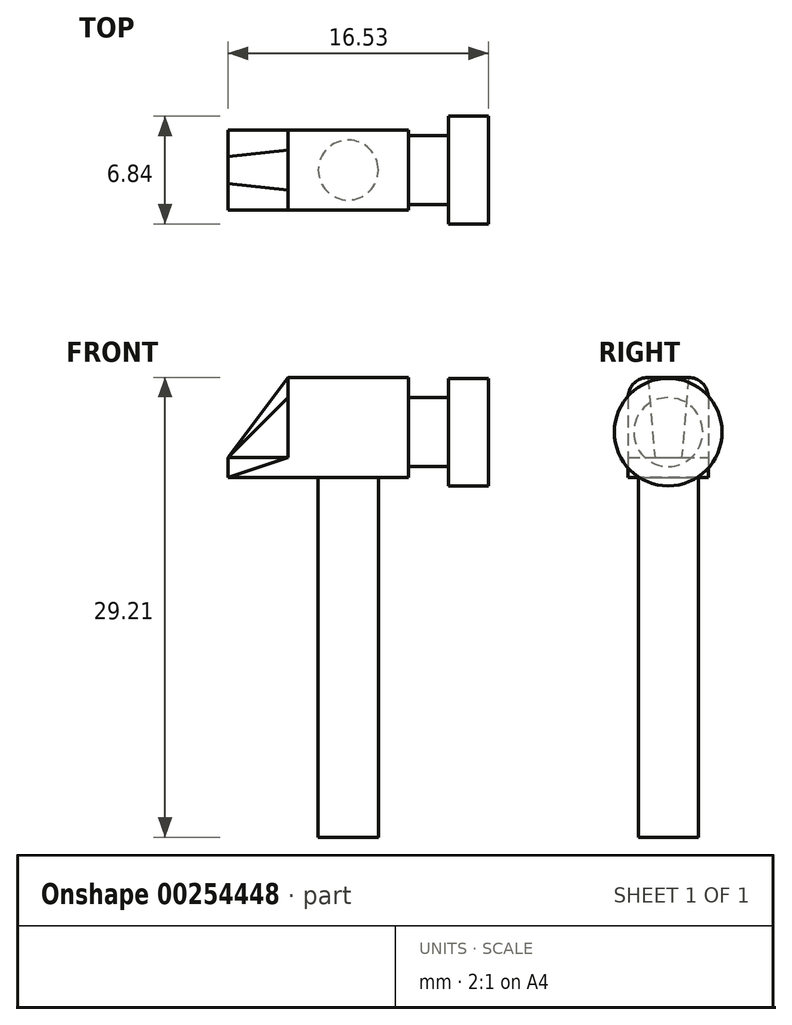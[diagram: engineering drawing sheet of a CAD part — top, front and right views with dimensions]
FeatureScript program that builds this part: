
annotation { "Feature Type Name" : "Feature", "Feature Type Description" : "" }
export const myFeature = defineFeature(function(context is Context, id is Id, definition is map)
    precondition{}
    {
        {
            var Q0;
            Q0=qCreatedBy(makeId("Front.planeOp"),FACE);
            var sketch = newSketch(context, id + "F0", { "sketchPlane" : qUnion([Q0])});
            skLineSegment(sketch, "E0.bottom", {"start": v(0, 0) * mm, "end": v(1.9, 0) * mm});
            skLineSegment(sketch, "E0.top", {"start": v(0, 22.86) * mm, "end": v(1.9, 22.86) * mm});
            skLineSegment(sketch, "E0.left", {"start": v(0, 0) * mm, "end": v(0, 22.86) * mm});
            skLineSegment(sketch, "E0.right", {"start": v(1.9, 0) * mm, "end": v(1.9, 22.86) * mm});
            skSolve(sketch);
        }
        {
            var Q0;
            Q0 = qSketchRegion(id + "F0", true);
            var Q1;
            Q1=sQuery(id+"F0.wireOp",EDGE,"E0.left");
            revolve(context, id + "F1", {"entities" : qUnion([Q0]), "axis" : qUnion([Q1]), "revolveType" : RevolveType.FULL});
        }
        {
            var Q0;
            Q0=makeQuery(id+"F1.opRevolve","SWEPT_FACE",FACE,{"disambiguationData":[OSD([sQuery(id+"F0.wireOp",EDGE,"E0.top")])]});
            var sketch = newSketch(context, id + "F2", { "sketchPlane" : qUnion([Q0])});
            skLineSegment(sketch, "E1.bottom", {"start": v(3.82, -2.55) * mm, "end": v(-3.82, -2.55) * mm});
            skLineSegment(sketch, "E1.top", {"start": v(3.82, 2.55) * mm, "end": v(-3.82, 2.55) * mm});
            skLineSegment(sketch, "E1.left", {"start": v(3.82, -2.55) * mm, "end": v(3.82, 2.55) * mm});
            skLineSegment(sketch, "E1.right", {"start": v(-3.82, -2.55) * mm, "end": v(-3.82, 2.55) * mm});
            skPoint(sketch, "E1.middle", {"position": v(0, 0) * mm});
            skSolve(sketch);
        }
        {
            var Q0;
            Q0 = qSketchRegion(id + "F2", true);
            extrude(context, id + "F3", {"entities" : qUnion([Q0]), "operationType" : NewBodyOperationType.ADD, "depth" : 6.35 * mm});
        }
        {
            var Q0;
            Q0=makeQuery(id+"F3.opExtrude","CAP_EDGE",EDGE,{"disambiguationData":[OSD([sQuery(id+"F2.wireOp",EDGE,"E1.bottom")])],"isStart":false});
            fillet(context, id + "F4", {"entities" : qUnion([Q0]), "radius" : 1.27 * mm, "tangentPropagation" : true, "allowEdgeOverflow" : false});
        }
        {
            var Q0;
            Q0=makeQuery(id+"F3.opExtrude","CAP_EDGE",EDGE,{"disambiguationData":[OSD([sQuery(id+"F2.wireOp",EDGE,"E1.top")])],"isStart":false});
            fillet(context, id + "F5", {"entities" : qUnion([Q0]), "radius" : 1.27 * mm, "tangentPropagation" : true, "allowEdgeOverflow" : false});
        }
        {
            var Q0;
            Q0=makeQuery(id+"F3.opExtrude","SWEPT_FACE",FACE,{"disambiguationData":[OSD([sQuery(id+"F2.wireOp",EDGE,"E1.left")])]});
            var sketch = newSketch(context, id + "F6", { "sketchPlane" : qUnion([Q0])});
            skSolve(sketch);
        }
        {
            var Q0;
            {var subQ0=sQuery(id+"F2.wireOp",EDGE,"E1.left");Q0=makeQuery(id+"F6.imprint","IMPRINT",FACE,{"disambiguationData":[TD([[makeQuery(id+"F6.imprint","IMPRINT",EDGE,{"derivedFrom":makeQuery(id+"F3.opExtrude","CAP_EDGE",EDGE,{"disambiguationData":[OSD([subQ0])],"isStart":true})}),1.0]])]});}
            var sketch = newSketch(context, id + "F7", { "sketchPlane" : qUnion([Q0])});
            skCircle(sketch, "E2", {"center": v(0, 25.74) * mm, "radius": 2.2 * mm});
            skSolve(sketch);
        }
        {
            var Q0;
            Q0 = qSketchRegion(id + "F7", true);
            extrude(context, id + "F8", {"entities" : qUnion([Q0]), "operationType" : NewBodyOperationType.ADD, "depth" : 2.54 * mm});
        }
        {
            var Q0;
            Q0=makeQuery(id+"F8.opExtrude","CAP_FACE",FACE,{"disambiguationData":[OSD([sQuery(id+"F7.wireOp",EDGE,"E2")])],"isStart":false});
            var sketch = newSketch(context, id + "F9", { "sketchPlane" : qUnion([Q0])});
            skCircle(sketch, "E3", {"center": v(0, 25.74) * mm, "radius": 3.42 * mm});
            skSolve(sketch);
        }
        {
            var Q0;
            Q0 = qSketchRegion(id + "F9", true);
            extrude(context, id + "F10", {"entities" : qUnion([Q0]), "operationType" : NewBodyOperationType.ADD, "depth" : 2.54 * mm});
        }
        {
            var Q0;
            Q0=makeQuery(id+"F3.opExtrude","SWEPT_FACE",FACE,{"disambiguationData":[OSD([sQuery(id+"F2.wireOp",EDGE,"E1.right")])]});
            var sketch = newSketch(context, id + "F11", { "sketchPlane" : qUnion([Q0])});
            skLineSegment(sketch, "E4.bottom", {"start": v(2.55, 22.86) * mm, "end": v(-2.55, 22.86) * mm});
            skLineSegment(sketch, "E4.top", {"start": v(2.55, 24.13) * mm, "end": v(-2.55, 24.13) * mm});
            skLineSegment(sketch, "E4.left", {"start": v(2.55, 22.86) * mm, "end": v(2.55, 24.13) * mm});
            skLineSegment(sketch, "E4.right", {"start": v(-2.55, 22.86) * mm, "end": v(-2.55, 24.13) * mm});
            skSolve(sketch);
        }
        {
            var Q0;
            Q0 = qSketchRegion(id + "F11", true);
            extrude(context, id + "F12", {"entities" : qUnion([Q0]), "operationType" : NewBodyOperationType.ADD, "depth" : 3.8 * mm});
        }
        {
            var Q0;
            Q0=makeQuery(id+"F3.opExtrude","SWEPT_FACE",FACE,{"disambiguationData":[OSD([sQuery(id+"F2.wireOp",EDGE,"E1.right")])]});
            var Q1;
            Q1=makeQuery(id+"F12.opExtrude","CAP_FACE",FACE,{"disambiguationData":[OSD([sQuery(id+"F11.wireOp",EDGE,"E4.bottom"),sQuery(id+"F11.wireOp",EDGE,"E4.top"),sQuery(id+"F11.wireOp",EDGE,"E4.left"),sQuery(id+"F11.wireOp",EDGE,"E4.right")])],"isStart":false});
            loft(context, id + "F13", {"sheetProfilesArray" : [{ "sheetProfileEntities" : qUnion([Q0]) }, { "sheetProfileEntities" : qUnion([Q1]) }]});
        }
    });
